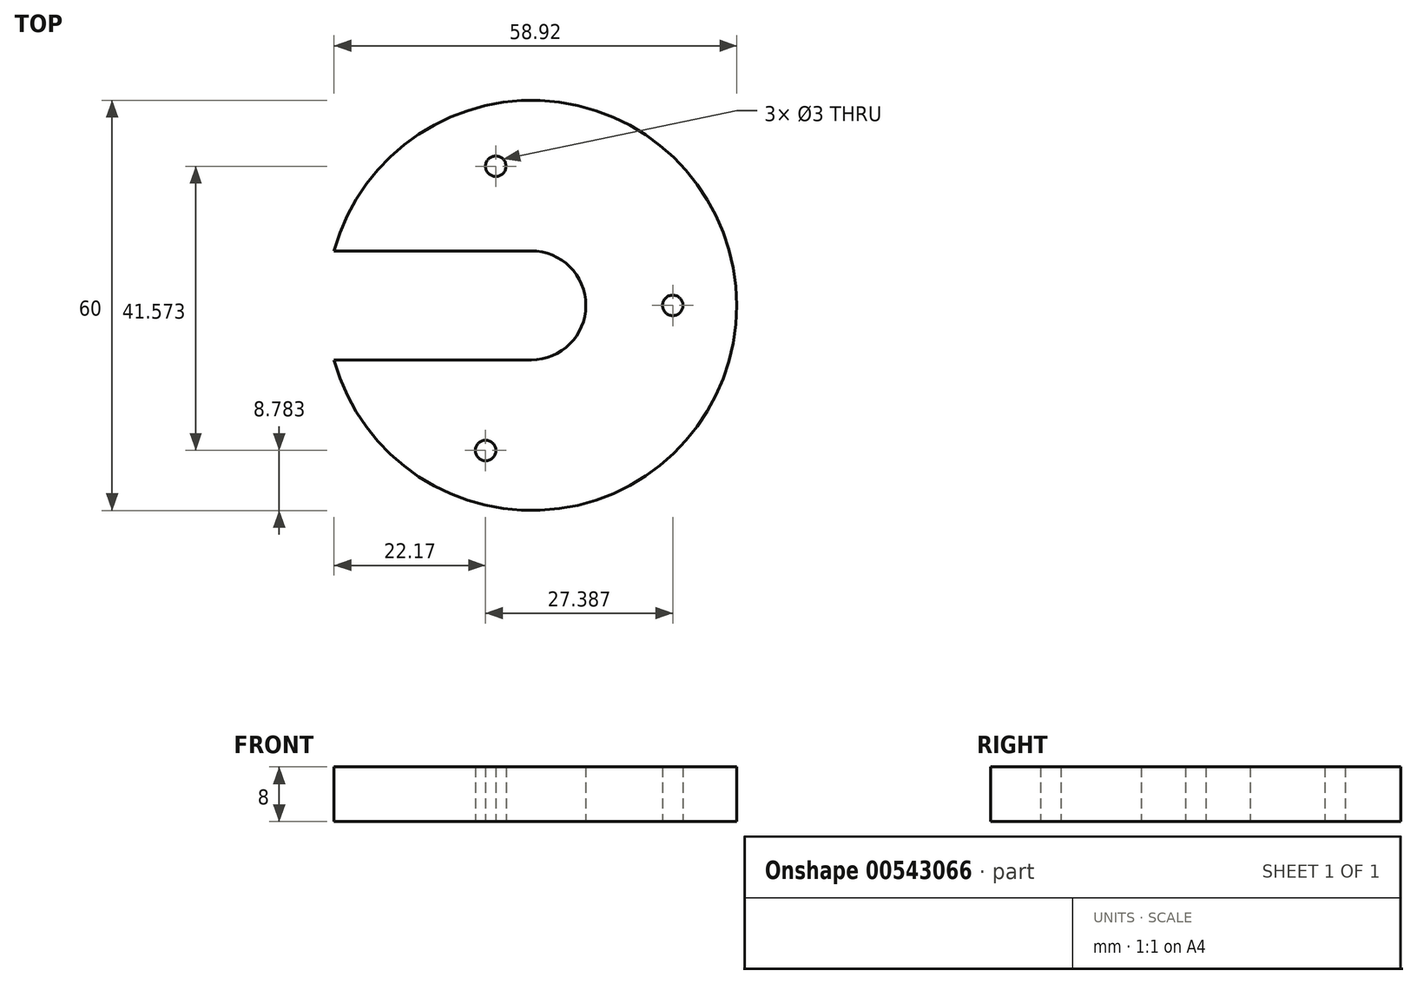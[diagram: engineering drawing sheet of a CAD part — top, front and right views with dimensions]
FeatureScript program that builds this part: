
annotation { "Feature Type Name" : "Feature", "Feature Type Description" : "" }
export const myFeature = defineFeature(function(context is Context, id is Id, definition is map)
    precondition{}
    {
        {
            var Q0;
            Q0=qCreatedBy(makeId("Top.planeOp"),FACE);
            var sketch = newSketch(context, id + "F0", { "sketchPlane" : qUnion([Q0])});
            skLineSegment(sketch, "E0", {"start": v(0, -7.98) * mm, "end": v(-28.85, -7.98) * mm});
            skLineSegment(sketch, "E1", {"start": v(0, 7.98) * mm, "end": v(-28.85, 7.98) * mm});
            skArc(sketch, "E2", {"start": v(-28.85, -7.98) * mm, "mid": v(30.07, 0) * mm, "end": v(-28.85, 7.98) * mm});
            skArc(sketch, "E3", {"start": v(0, -7.98) * mm, "mid": v(7.98, 0) * mm, "end": v(0, 7.98) * mm});
            skCircle(sketch, "E4", {"center": v(-6.68, -21.22) * mm, "radius": 1.5 * mm});
            skCircle(sketch, "E5", {"center": v(20.7, 0) * mm, "radius": 1.5 * mm});
            skCircle(sketch, "E6", {"center": v(-5.19, 20.36) * mm, "radius": 1.5 * mm});
            skSolve(sketch);
        }
        {
            var Q0;
            Q0 = qSketchRegion(id + "F0", true);
            extrude(context, id + "F1", {"entities" : qUnion([Q0]), "depth" : 8 * mm, "offsetDistance" : 25 * mm});
        }
    });
